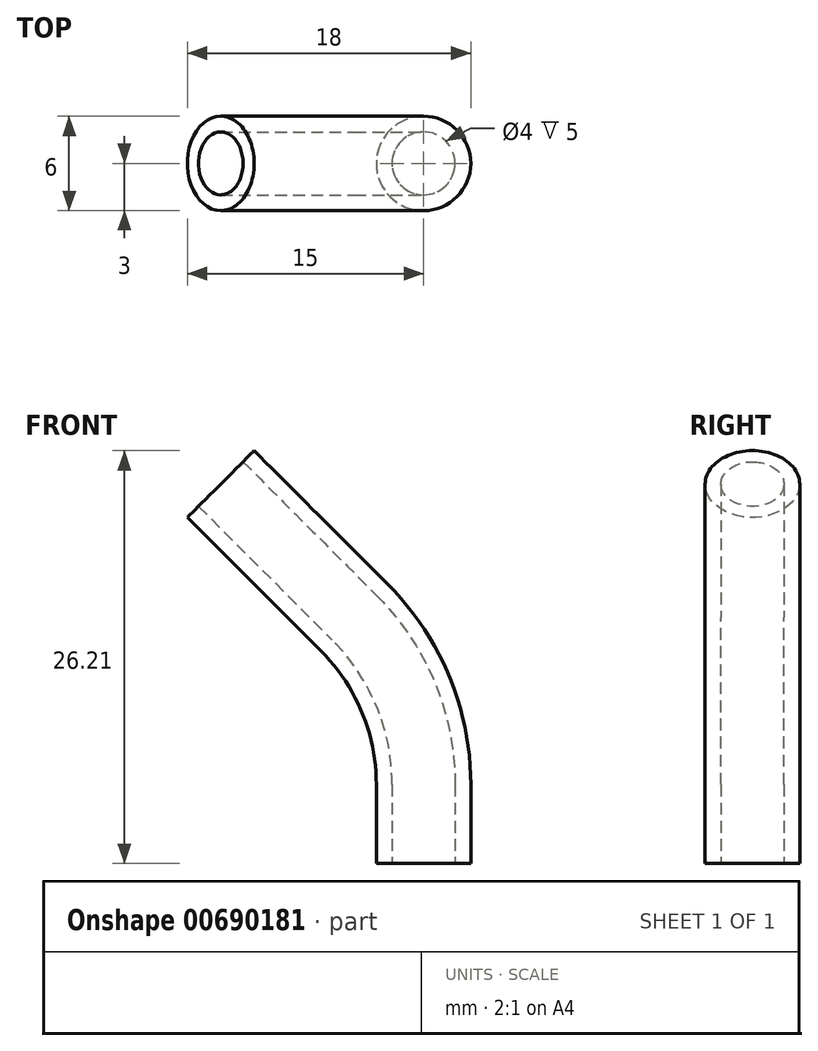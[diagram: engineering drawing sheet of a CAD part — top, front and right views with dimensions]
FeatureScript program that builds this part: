
annotation { "Feature Type Name" : "Feature", "Feature Type Description" : "" }
export const myFeature = defineFeature(function(context is Context, id is Id, definition is map)
    precondition{}
    {
        {
            var Q0;
            Q0=qCreatedBy(makeId("Front.planeOp"),FACE);
            var sketch = newSketch(context, id + "F0", { "sketchPlane" : qUnion([Q0])});
            skArc(sketch, "E0", {"start": v(0, 0) * mm, "mid": v(-1.14, 5.74) * mm, "end": v(-4.4, 10.6) * mm});
            skLineSegment(sketch, "E1", {"start": v(-4.4, 10.6) * mm, "end": v(-12.88, 19.1) * mm});
            skLineSegment(sketch, "E2", {"start": v(0, 0) * mm, "end": v(0, -5) * mm});
            skLineSegment(sketch, "E3", {"start": v(-15, 21.21) * mm, "end": v(-15, 8.37) * mm, "construction": true});
            skLineSegment(sketch, "E4", {"start": v(-12.88, 19.1) * mm, "end": v(-15, 21.21) * mm, "construction": true});
            skSolve(sketch);
        }
        {
            var Q0;
            Q0=qCreatedBy(makeId("Top.planeOp"),FACE);
            var sketch = newSketch(context, id + "F1", { "sketchPlane" : qUnion([Q0])});
            skCircle(sketch, "E5", {"center": v(0, 0) * mm, "radius": 2 * mm});
            skCircle(sketch, "E6", {"center": v(0, 0) * mm, "radius": 3 * mm});
            skSolve(sketch);
        }
        {
            var Q0;
            Q0 = qSketchRegion(id + "F1", true);
            var Q1;
            Q1 = qConstructionFilter(qBodyType(qCreatedBy(id + "F0" ,EDGE), BodyType.WIRE), ConstructionObject.NO);
            sweep(context, id + "F2", {"profiles" : qUnion([Q0]), "path" : qUnion([Q1])});
        }
    });
